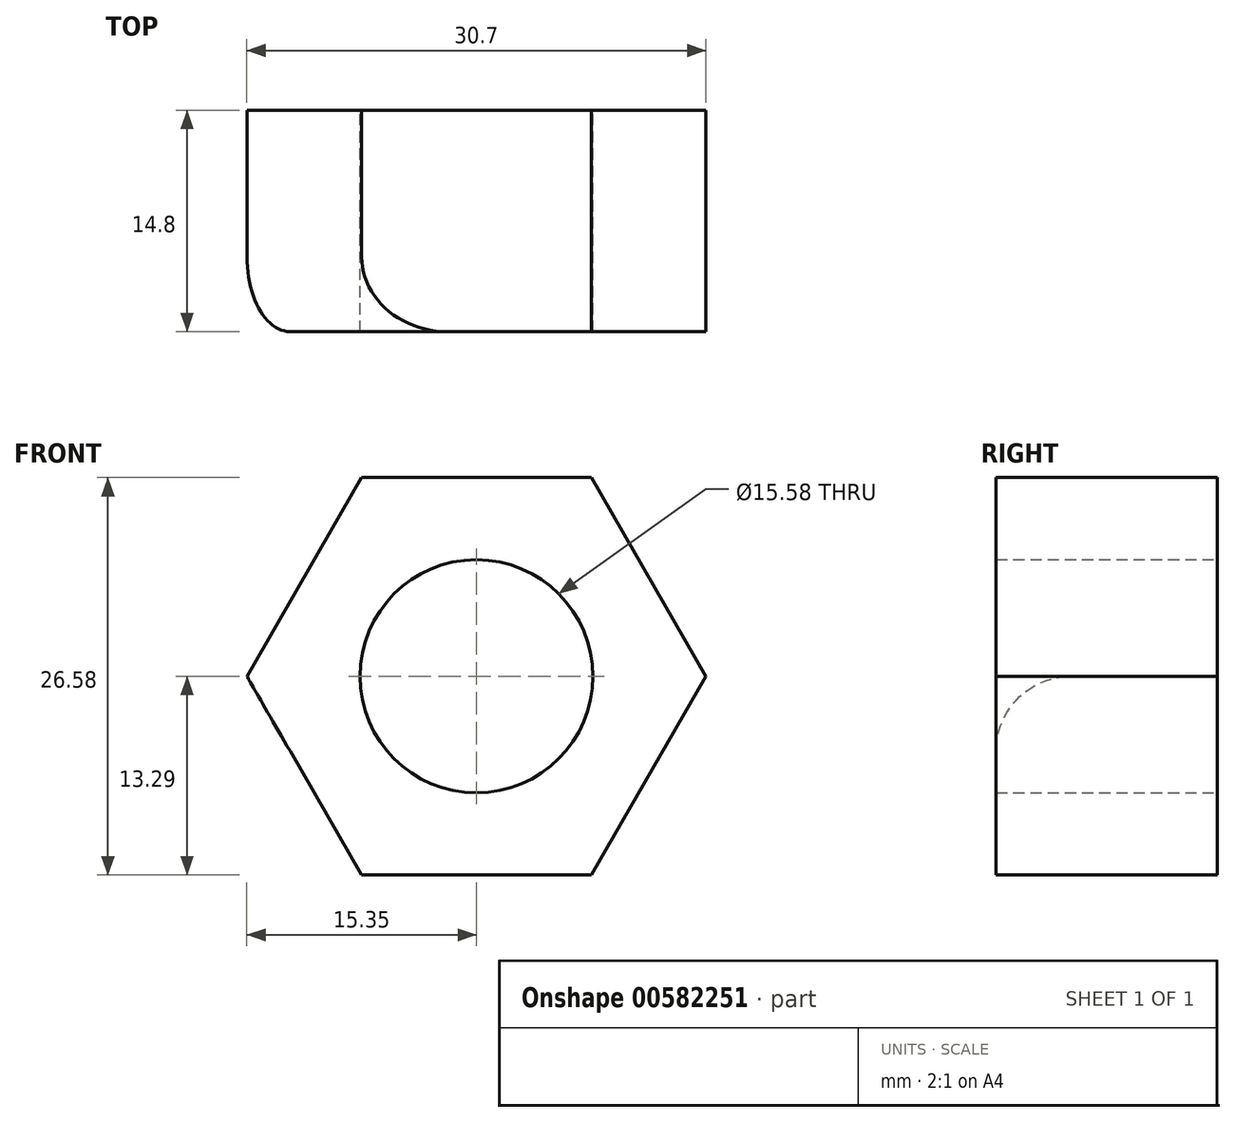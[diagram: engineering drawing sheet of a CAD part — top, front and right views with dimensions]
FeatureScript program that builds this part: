
annotation { "Feature Type Name" : "Feature", "Feature Type Description" : "" }
export const myFeature = defineFeature(function(context is Context, id is Id, definition is map)
    precondition{}
    {
        {
            var Q0;
            Q0=qCreatedBy(makeId("Front.planeOp"),FACE);
            var sketch = newSketch(context, id + "F0", { "sketchPlane" : qUnion([Q0])});
            skLineSegment(sketch, "E0.0", {"start": v(-7.67, 13.29) * mm, "end": v(7.67, 13.29) * mm});
            skLineSegment(sketch, "E0.1", {"start": v(7.67, 13.29) * mm, "end": v(15.35, 0) * mm});
            skLineSegment(sketch, "E0.2", {"start": v(15.35, 0) * mm, "end": v(7.67, -13.29) * mm});
            skLineSegment(sketch, "E0.3", {"start": v(7.67, -13.29) * mm, "end": v(-7.67, -13.3) * mm});
            skLineSegment(sketch, "E0.4", {"start": v(-7.67, -13.3) * mm, "end": v(-15.35, 0) * mm});
            skLineSegment(sketch, "E0.5", {"start": v(-15.35, 0) * mm, "end": v(-7.67, 13.29) * mm});
            skPoint(sketch, "E0.0.midPoint", {"position": v(0, 13.29) * mm});
            skCircle(sketch, "E1", {"center": v(0, 0) * mm, "radius": 7.79 * mm});
            skSolve(sketch);
        }
        {
            var Q0;
            Q0 = qSketchRegion(id + "F0", true);
            extrude(context, id + "F1", {"entities" : qUnion([Q0]), "depth" : 14.8 * mm, "offsetDistance" : 25 * mm});
        }
        {
            var Q0;
            Q0=makeQuery(id+"F1.opExtrude","CAP_EDGE",EDGE,{"disambiguationData":[OSD([sQuery(id+"F0.wireOp",EDGE,"E0.5")])],"isStart":false});
            fillet(context, id + "F2", {"entities" : qUnion([Q0]), "radius" : 5 * mm, "tangentPropagation" : true, "allowEdgeOverflow" : false});
        }
    });
